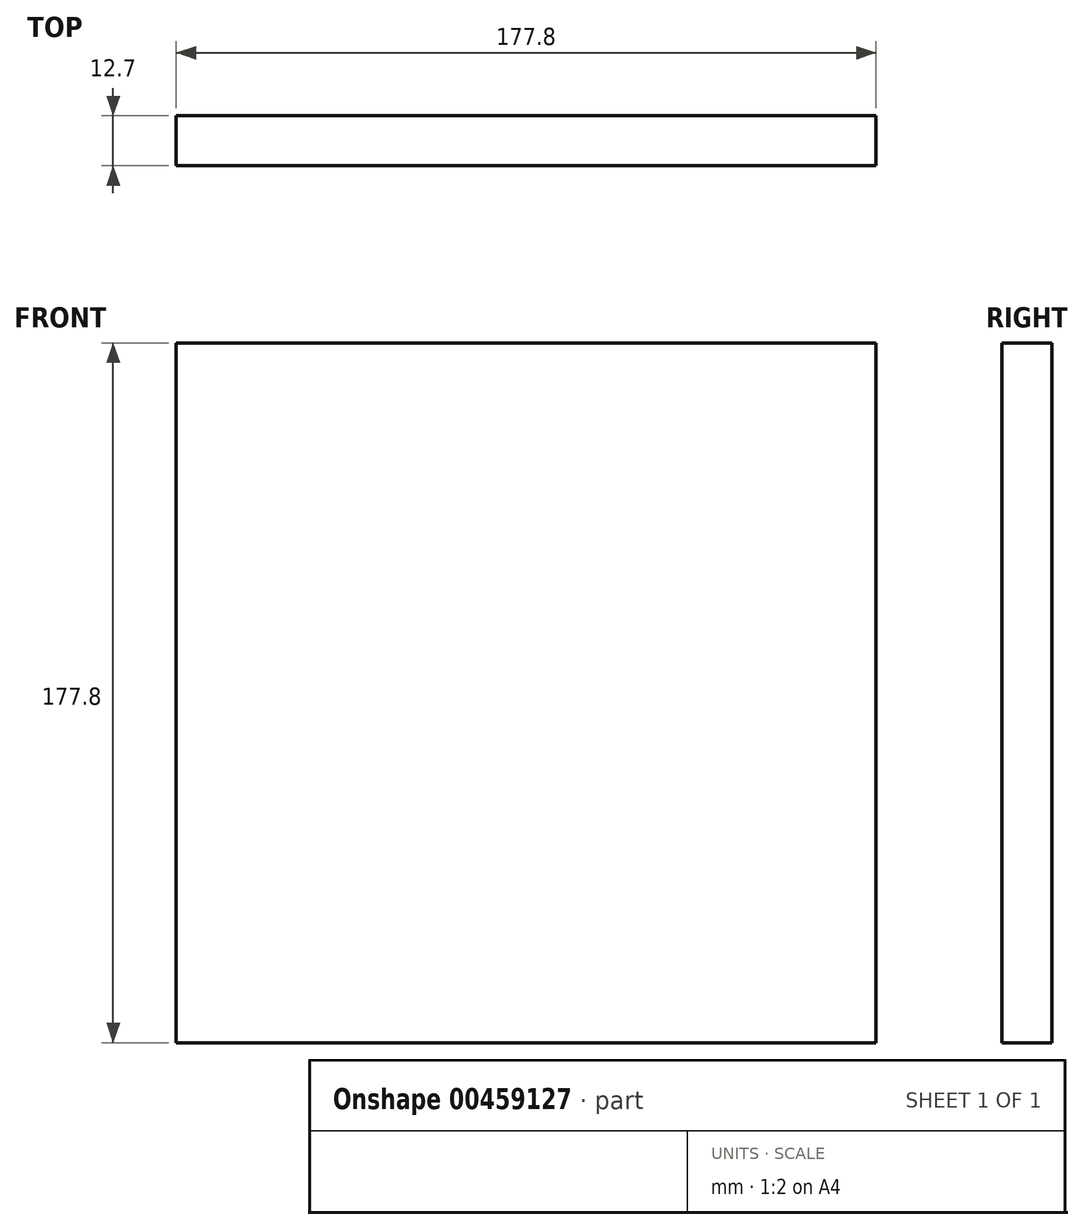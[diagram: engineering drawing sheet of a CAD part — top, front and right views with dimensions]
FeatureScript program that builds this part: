
annotation { "Feature Type Name" : "Feature", "Feature Type Description" : "" }
export const myFeature = defineFeature(function(context is Context, id is Id, definition is map)
    precondition{}
    {
        {
            var Q0;
            Q0=qCreatedBy(makeId("Front.planeOp"),FACE);
            var sketch = newSketch(context, id + "F0", { "sketchPlane" : qUnion([Q0])});
            skLineSegment(sketch, "E0.bottom", {"start": v(0, 0) * mm, "end": v(-177.8, 0) * mm});
            skLineSegment(sketch, "E0.top", {"start": v(0, 177.8) * mm, "end": v(-177.8, 177.8) * mm});
            skLineSegment(sketch, "E0.left", {"start": v(0, 0) * mm, "end": v(0, 177.8) * mm});
            skLineSegment(sketch, "E0.right", {"start": v(-177.8, 0) * mm, "end": v(-177.8, 177.8) * mm});
            skSolve(sketch);
        }
        {
            var Q0;
            Q0=makeQuery(id+"F0.imprint","IMPRINT",FACE,{"disambiguationData":[TD([[makeQuery(id+"F0.imprint","IMPRINT",EDGE,{"derivedFrom":sQuery(id+"F0.wireOp",EDGE,"E0.bottom")}),-1.0]])]});
            extrude(context, id + "F1", {"entities" : qUnion([Q0]), "depth" : 12.7 * mm});
        }
    });
